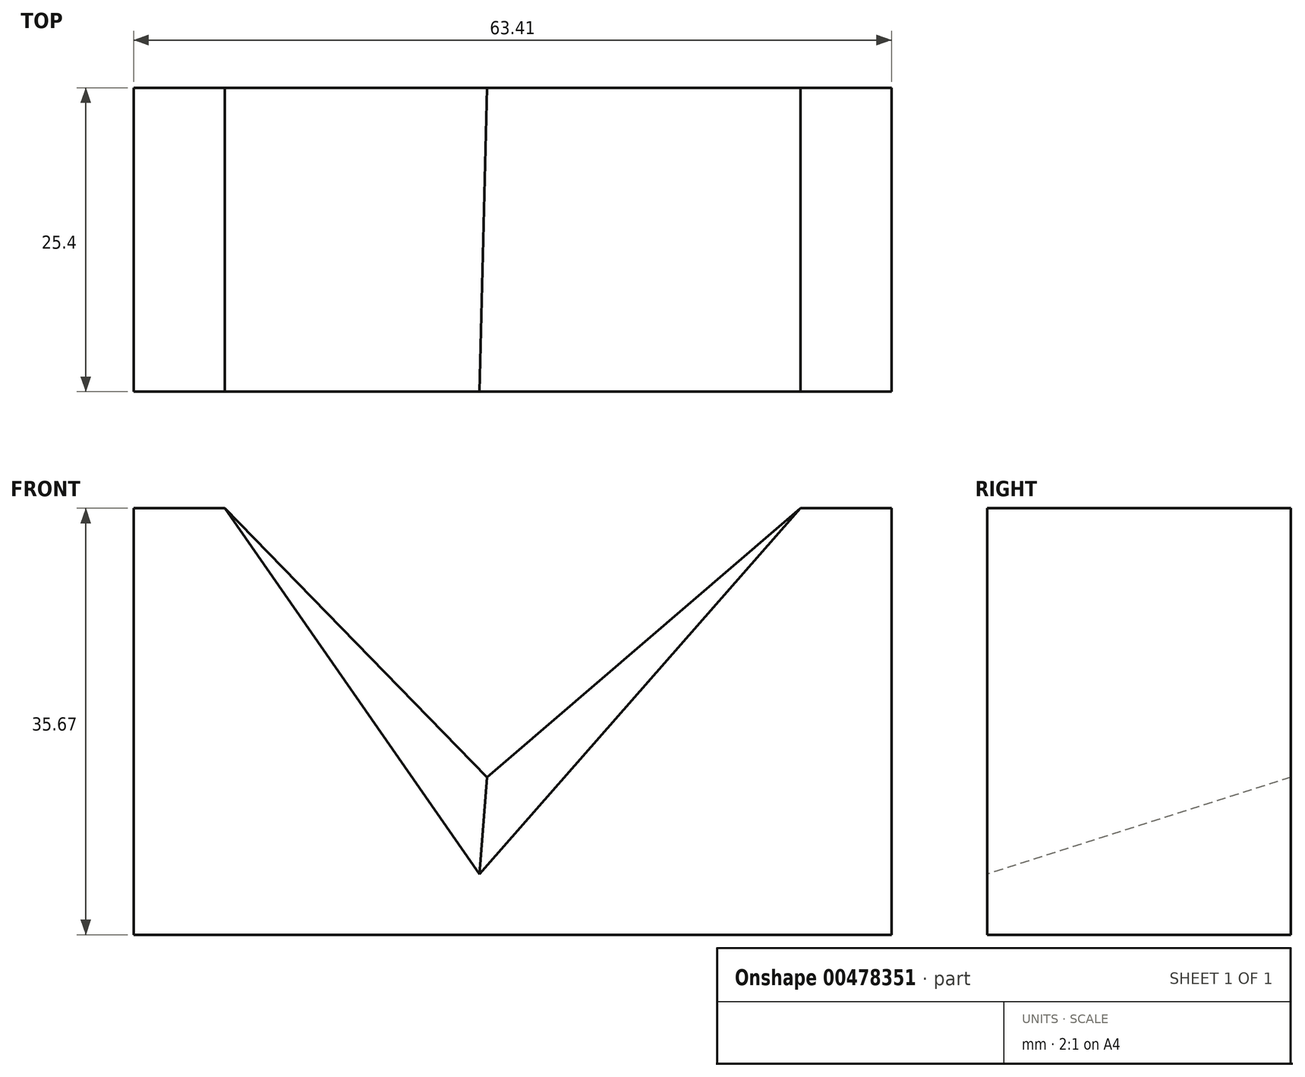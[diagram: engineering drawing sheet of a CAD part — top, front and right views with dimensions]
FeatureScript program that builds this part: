
annotation { "Feature Type Name" : "Feature", "Feature Type Description" : "" }
export const myFeature = defineFeature(function(context is Context, id is Id, definition is map)
    precondition{}
    {
        {
            var Q0;
            Q0=qCreatedBy(makeId("Front.planeOp"),FACE);
            var sketch = newSketch(context, id + "F0", { "sketchPlane" : qUnion([Q0])});
            skLineSegment(sketch, "E0.bottom", {"start": v(0, 0) * mm, "end": v(63.41, 0) * mm});
            skLineSegment(sketch, "E0.top", {"start": v(0, 35.67) * mm, "end": v(63.41, 35.67) * mm});
            skLineSegment(sketch, "E0.left", {"start": v(0, 0) * mm, "end": v(0, 35.67) * mm});
            skLineSegment(sketch, "E0.right", {"start": v(63.41, 0) * mm, "end": v(63.41, 35.67) * mm});
            skSolve(sketch);
        }
        {
            var Q0;
            Q0 = qSketchRegion(id + "F0", true);
            extrude(context, id + "F1", {"entities" : qUnion([Q0]), "depth" : 25.4 * mm});
        }
        {
            var Q0;
            Q0=makeQuery(id+"F1.opExtrude","CAP_FACE",FACE,{"disambiguationData":[OSD([sQuery(id+"F0.wireOp",EDGE,"E0.bottom"),sQuery(id+"F0.wireOp",EDGE,"E0.top"),sQuery(id+"F0.wireOp",EDGE,"E0.left"),sQuery(id+"F0.wireOp",EDGE,"E0.right")])],"isStart":false});
            var sketch = newSketch(context, id + "F2", { "sketchPlane" : qUnion([Q0])});
            skLineSegment(sketch, "E1", {"start": v(7.62, 35.67) * mm, "end": v(55.8, 35.67) * mm});
            skLineSegment(sketch, "E2", {"start": v(55.8, 35.67) * mm, "end": v(28.94, 5.06) * mm});
            skLineSegment(sketch, "E3", {"start": v(28.94, 5.06) * mm, "end": v(7.62, 35.67) * mm});
            skSolve(sketch);
        }
        {
            var Q0;
            Q0=makeQuery(id+"F1.opExtrude","CAP_FACE",FACE,{"disambiguationData":[OSD([sQuery(id+"F0.wireOp",EDGE,"E0.bottom"),sQuery(id+"F0.wireOp",EDGE,"E0.top"),sQuery(id+"F0.wireOp",EDGE,"E0.left"),sQuery(id+"F0.wireOp",EDGE,"E0.right")])],"isStart":true});
            var sketch = newSketch(context, id + "F3", { "sketchPlane" : qUnion([Q0])});
            skLineSegment(sketch, "E4", {"start": v(-55.8, 35.67) * mm, "end": v(-7.62, 35.67) * mm});
            skLineSegment(sketch, "E5", {"start": v(-7.62, 35.67) * mm, "end": v(-29.57, 13.17) * mm});
            skLineSegment(sketch, "E6", {"start": v(-29.57, 13.17) * mm, "end": v(-55.8, 35.67) * mm});
            skSolve(sketch);
        }
        {
            var Q1;
            Q1=makeQuery(id+"F3.imprint","IMPRINT",FACE,{"disambiguationData":[TD([[makeQuery(id+"F3.imprint","IMPRINT",EDGE,{"derivedFrom":sQuery(id+"F3.wireOp",EDGE,"E4")}),1.0]])]});
            var Q2;
            Q2=makeQuery(id+"F2.imprint","IMPRINT",FACE,{"disambiguationData":[TD([[makeQuery(id+"F2.imprint","IMPRINT",EDGE,{"derivedFrom":sQuery(id+"F2.wireOp",EDGE,"E1")}),-1.0]])]});
            loft(context, id + "F4", {"operationType" : NewBodyOperationType.REMOVE, "sheetProfilesArray" : [{ "sheetProfileEntities" : qUnion([Q1]) }, { "sheetProfileEntities" : qUnion([Q2]) }]});
        }
    });
